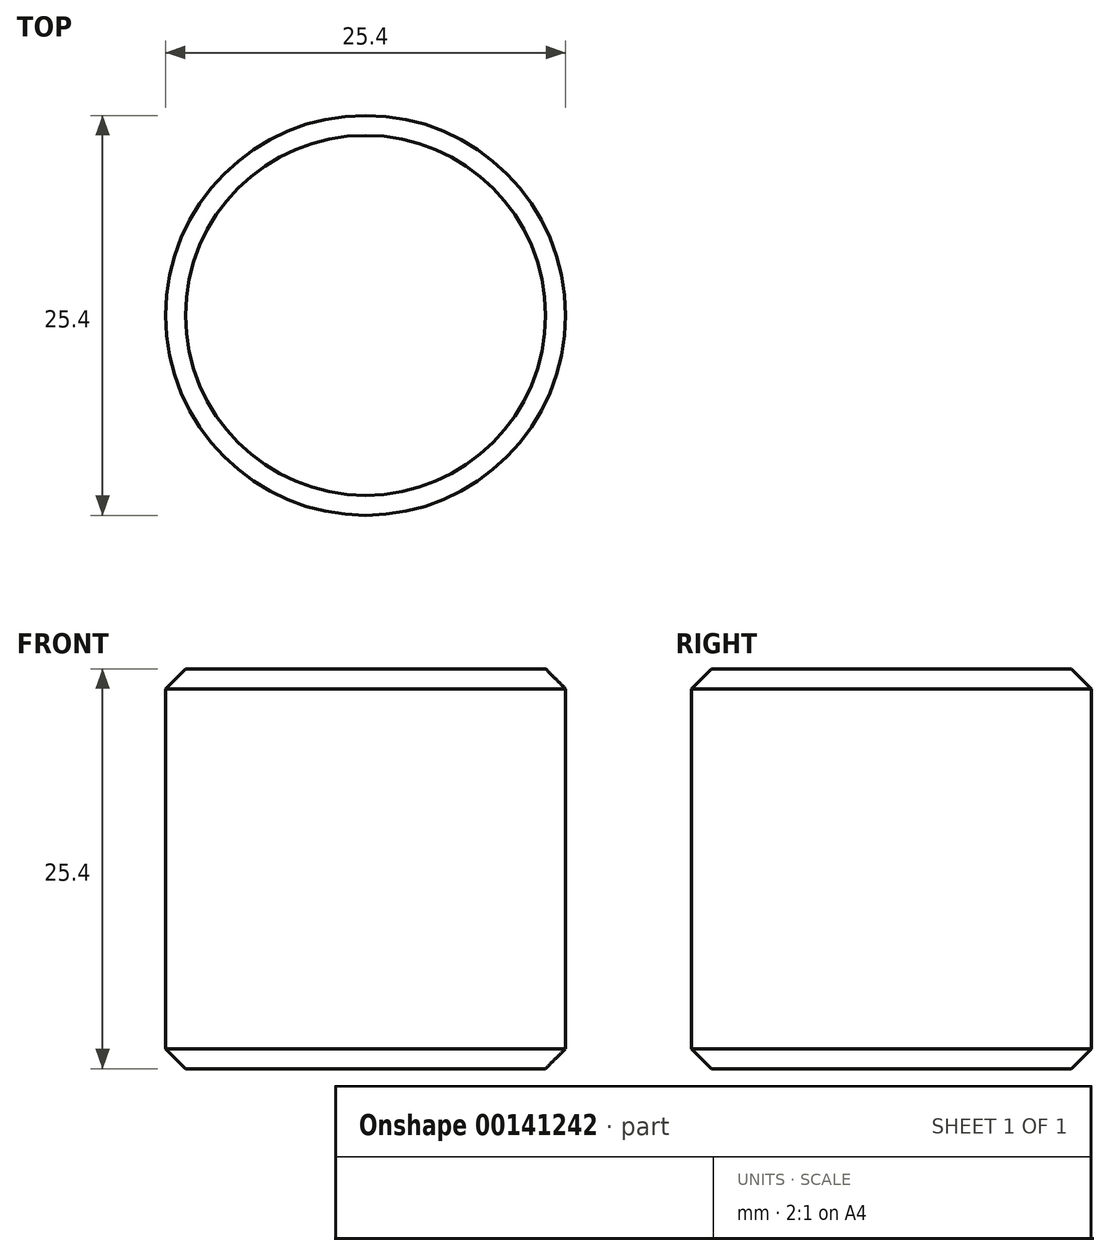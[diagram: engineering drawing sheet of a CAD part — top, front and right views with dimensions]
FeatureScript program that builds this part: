
annotation { "Feature Type Name" : "Feature", "Feature Type Description" : "" }
export const myFeature = defineFeature(function(context is Context, id is Id, definition is map)
    precondition{}
    {
        {
            var Q0;
            Q0=qCreatedBy(makeId("Top.planeOp"),FACE);
            var sketch = newSketch(context, id + "F0", { "sketchPlane" : qUnion([Q0])});
            skCircle(sketch, "E0", {"center": v(0, 0) * mm, "radius": 12.7 * mm});
            skSolve(sketch);
        }
        {
            var Q0;
            Q0 = qSketchRegion(id + "F0", true);
            extrude(context, id + "F1", {"entities" : qUnion([Q0]), "depth" : 25.4 * mm});
        }
        {
            var Q0;
            Q0=makeQuery(id+"F1.opExtrude","CAP_EDGE",EDGE,{"disambiguationData":[OSD([sQuery(id+"F0.wireOp",EDGE,"E0")])],"isStart":false});
            chamfer(context, id + "F2", {"entities" : qUnion([Q0]), "width" : 1.27 * mm, "tangentPropagation" : true});
        }
        {
            var Q0;
            Q0=makeQuery(id+"F1.opExtrude","CAP_EDGE",EDGE,{"disambiguationData":[OSD([sQuery(id+"F0.wireOp",EDGE,"E0")])],"isStart":true});
            chamfer(context, id + "F3", {"entities" : qUnion([Q0]), "width" : 1.27 * mm, "tangentPropagation" : true});
        }
    });
